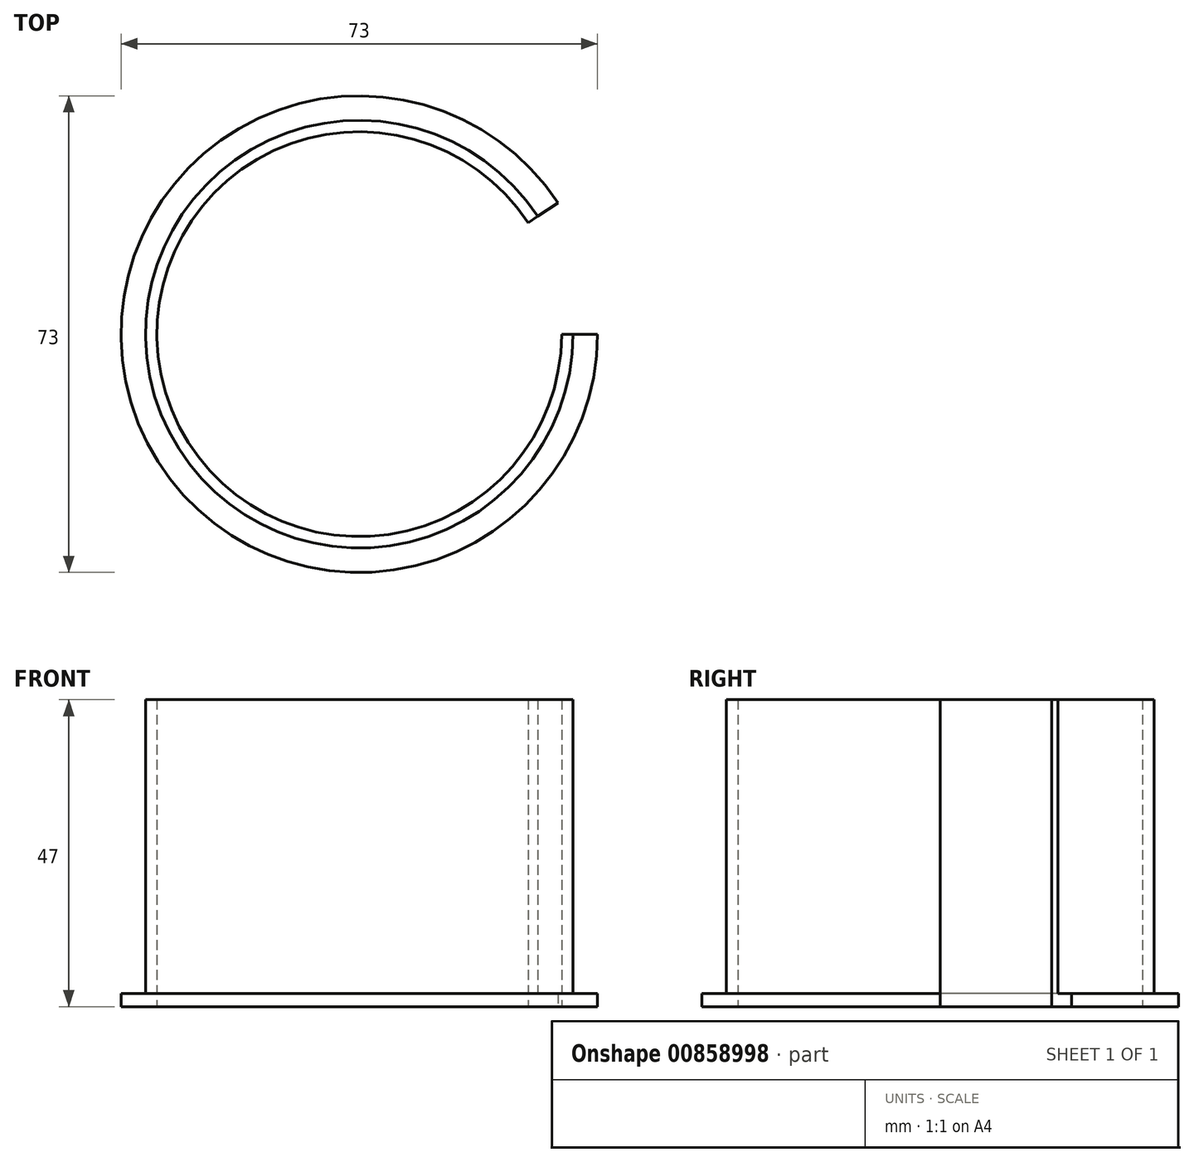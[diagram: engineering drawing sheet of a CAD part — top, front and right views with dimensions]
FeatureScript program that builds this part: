
annotation { "Feature Type Name" : "Feature", "Feature Type Description" : "" }
export const myFeature = defineFeature(function(context is Context, id is Id, definition is map)
    precondition{}
    {
        {
            var Q0;
            Q0=qCreatedBy(makeId("Top.planeOp"),FACE);
            var sketch = newSketch(context, id + "F0", { "sketchPlane" : qUnion([Q0])});
            skCircle(sketch, "E0", {"center": v(0, 0) * mm, "radius": 31 * mm});
            skCircle(sketch, "E1", {"center": v(0, 0) * mm, "radius": 32.75 * mm});
            skSolve(sketch);
        }
        {
            var Q0;
            Q0=qSketchRegion(id+"F0",true);
            extrude(context, id + "F1", {"entities" : qUnion([Q0]), "depth" : 47 * mm, "offsetDistance" : 25 * mm});
        }
        {
            var Q0;
            Q0=qCreatedBy(makeId("Top.planeOp"),FACE);
            var sketch = newSketch(context, id + "F2", { "sketchPlane" : qUnion([Q0])});
            skCircle(sketch, "E2", {"center": v(0, 0) * mm, "radius": 36.5 * mm});
            skCircle(sketch, "E3", {"center": v(0, 0) * mm, "radius": 31 * mm});
            skSolve(sketch);
        }
        {
            var Q0;
            Q0=qSketchRegion(id+"F2",true);
            extrude(context, id + "F3", {"entities" : qUnion([Q0]), "operationType" : NewBodyOperationType.ADD, "depth" : 2 * mm, "offsetDistance" : 25 * mm});
        }
        {
            var Q0;
            Q0=qCreatedBy(makeId("Top.planeOp"),FACE);
            var sketch = newSketch(context, id + "F4", { "sketchPlane" : qUnion([Q0])});
            skLineSegment(sketch, "E4", {"start": v(0, 0) * mm, "end": v(36.5, 0) * mm, "construction": true});
            skLineSegment(sketch, "E5", {"start": v(0, 0) * mm, "end": v(30.46, 20.11) * mm, "construction": true});
            skLineSegment(sketch, "E6", {"start": v(30.46, 20.11) * mm, "end": v(25.87, 17.08) * mm});
            skLineSegment(sketch, "E7", {"start": v(36.5, 0) * mm, "end": v(31, 0) * mm});
            skArc(sketch, "E8", {"start": v(36.5, 0) * mm, "mid": v(34.96, 10.5) * mm, "end": v(30.46, 20.11) * mm});
            skArc(sketch, "E9", {"start": v(31, 0) * mm, "mid": v(29.69, 8.92) * mm, "end": v(25.87, 17.08) * mm});
            skSolve(sketch);
        }
        {
            var Q0;
            Q0=qSketchRegion(id+"F4",true);
            extrude(context, id + "F5", {"entities" : qUnion([Q0]), "operationType" : NewBodyOperationType.REMOVE, "endBound" : BoundingType.UP_TO_NEXT, "depth" : 25 * mm, "offsetDistance" : 25 * mm});
        }
    });
